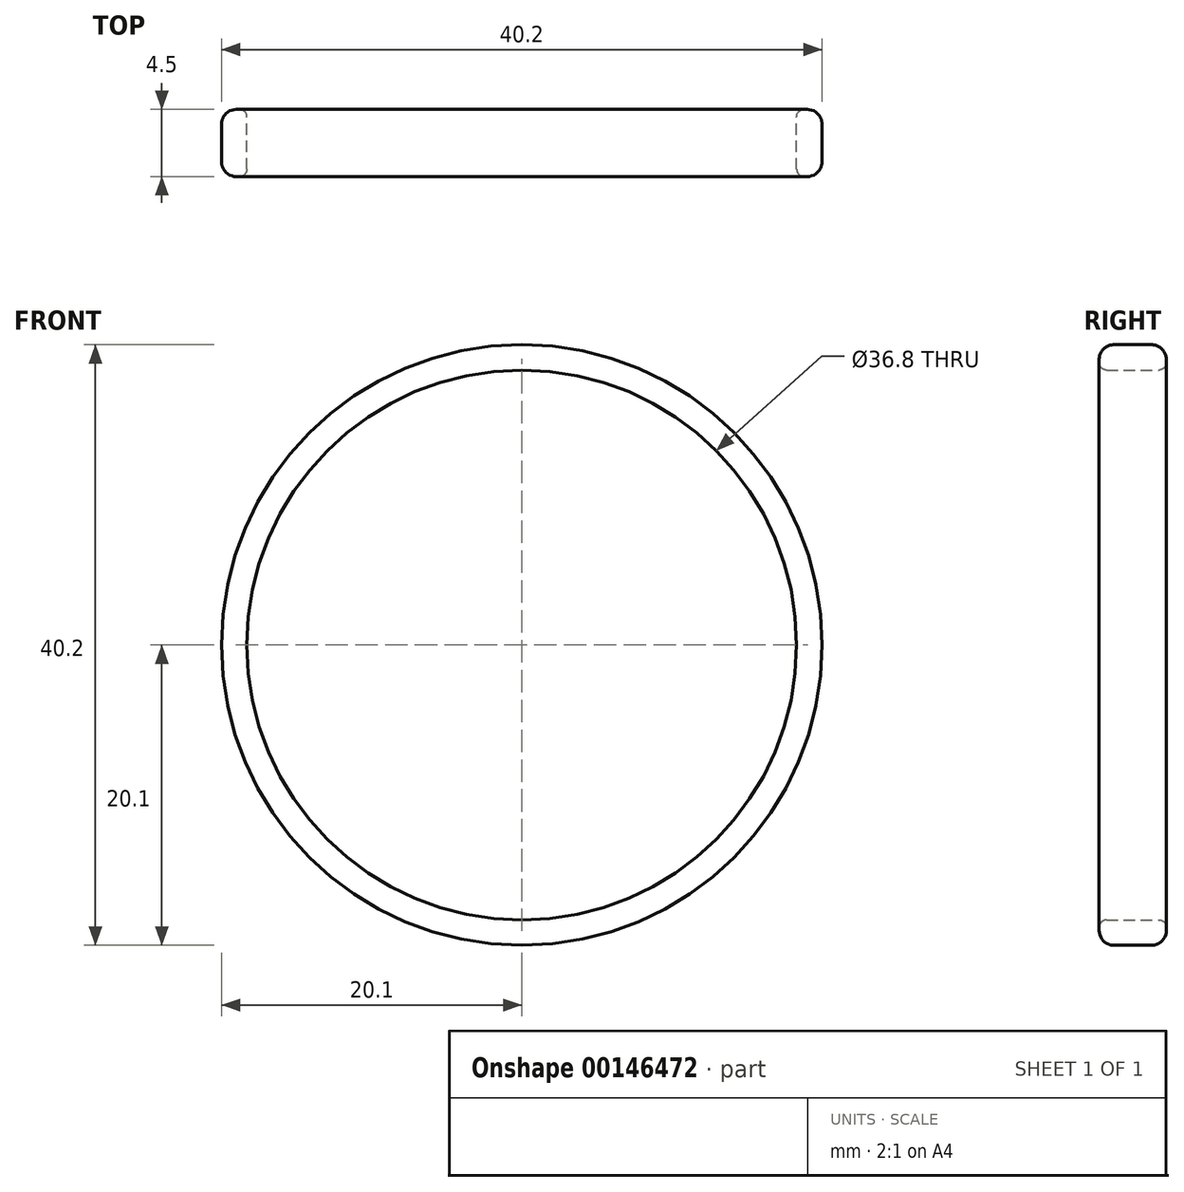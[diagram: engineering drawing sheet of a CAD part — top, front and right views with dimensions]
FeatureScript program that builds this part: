
annotation { "Feature Type Name" : "Feature", "Feature Type Description" : "" }
export const myFeature = defineFeature(function(context is Context, id is Id, definition is map)
    precondition{}
    {
        {
            var Q0;
            Q0=qCreatedBy(makeId("Top.planeOp"),FACE);
            var sketch = newSketch(context, id + "F0", { "sketchPlane" : qUnion([Q0])});
            skLineSegment(sketch, "E0", {"start": v(0, 0) * mm, "end": v(-18.4, 0) * mm});
            skLineSegment(sketch, "E1.bottom", {"start": v(-18.4, 0) * mm, "end": v(-20.1, 0) * mm});
            skLineSegment(sketch, "E1.top", {"start": v(-18.9, 2.25) * mm, "end": v(-19.1, 2.25) * mm});
            skLineSegment(sketch, "E1.left", {"start": v(-18.4, 0) * mm, "end": v(-18.4, 1.75) * mm});
            skLineSegment(sketch, "E1.right", {"start": v(-20.1, 0) * mm, "end": v(-20.1, 1.25) * mm});
            skLineSegment(sketch, "E2.MirrorCS", {"start": v(-18.9, -2.25) * mm, "end": v(-19.1, -2.25) * mm});
            skLineSegment(sketch, "E3.MirrorCS", {"start": v(-20.1, 0) * mm, "end": v(-20.1, -1.25) * mm});
            skLineSegment(sketch, "E4.MirrorCS", {"start": v(-18.4, 0) * mm, "end": v(-18.4, -1.75) * mm});
            skLineSegment(sketch, "E5", {"start": v(-18.9, 2.25) * mm, "end": v(-18.9, -2.25) * mm});
            skPoint(sketch, "E6.visualSharp", {"position": v(-18.4, -2.25) * mm});
            skArc(sketch, "E6.filletArc", {"start": v(-18.9, -2.25) * mm, "mid": v(-18.55, -2.1) * mm, "end": v(-18.4, -1.75) * mm});
            skPoint(sketch, "E7.visualSharp", {"position": v(-18.4, 2.25) * mm});
            skArc(sketch, "E7.filletArc", {"start": v(-18.4, 1.75) * mm, "mid": v(-18.55, 2.1) * mm, "end": v(-18.9, 2.25) * mm});
            skPoint(sketch, "E8.visualSharp", {"position": v(-20.1, 2.25) * mm});
            skArc(sketch, "E8.filletArc", {"start": v(-19.1, 2.25) * mm, "mid": v(-19.8, 1.96) * mm, "end": v(-20.1, 1.25) * mm});
            skPoint(sketch, "E9.visualSharp", {"position": v(-20.1, -2.25) * mm});
            skArc(sketch, "E9.filletArc", {"start": v(-20.1, -1.25) * mm, "mid": v(-19.8, -1.96) * mm, "end": v(-19.1, -2.25) * mm});
            skLineSegment(sketch, "E10", {"start": v(0, 0) * mm, "end": v(0, -10.7) * mm});
            skSolve(sketch);
        }
        {
            var Q0;
            {var subQ1=sQuery(id+"F0.wireOp",EDGE,"E1.top");Q0=makeQuery(id+"F0.imprint","IMPRINT",FACE,{"disambiguationData":[TD([[makeQuery(id+"F0.imprint","IMPRINT",EDGE,{"derivedFrom":subQ1}),1.0]])]});}
            var Q1;
            {var subQ0=sQuery(id+"F0.wireOp",EDGE,"E4.MirrorCS");Q1=makeQuery(id+"F0.imprint","IMPRINT",FACE,{"disambiguationData":[TD([[makeQuery(id+"F0.imprint","IMPRINT",EDGE,{"derivedFrom":subQ0}),-1.0]])]});}
            var Q2;
            {var subQ0=sQuery(id+"F0.wireOp",EDGE,"E1.left");Q2=makeQuery(id+"F0.imprint","IMPRINT",FACE,{"disambiguationData":[TD([[makeQuery(id+"F0.imprint","IMPRINT",EDGE,{"derivedFrom":subQ0}),1.0]])]});}
            var Q3;
            {var subQ1=sQuery(id+"F0.wireOp",EDGE,"E2.MirrorCS");Q3=makeQuery(id+"F0.imprint","IMPRINT",FACE,{"disambiguationData":[TD([[makeQuery(id+"F0.imprint","IMPRINT",EDGE,{"derivedFrom":subQ1}),-1.0]])]});}
            var Q4;
            Q4=sQuery(id+"F0.wireOp",EDGE,"E10");
            revolve(context, id + "F1", {"entities" : qUnion([Q0, Q1, Q2, Q3]), "axis" : qUnion([Q4]), "revolveType" : RevolveType.FULL});
        }
    });
